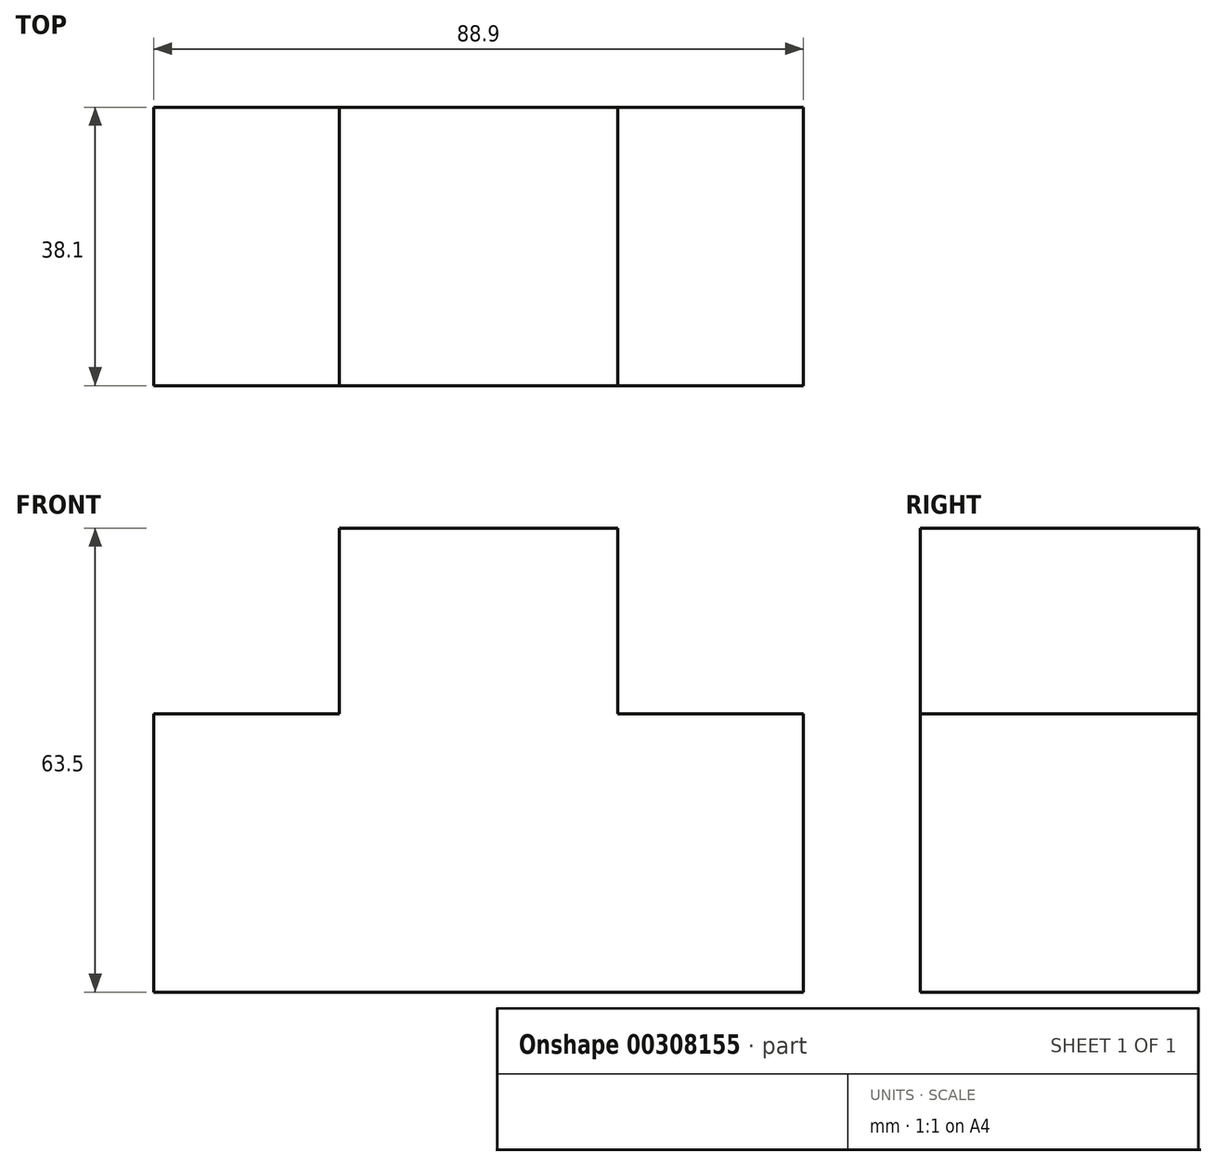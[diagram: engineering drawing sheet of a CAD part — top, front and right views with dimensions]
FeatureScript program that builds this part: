
annotation { "Feature Type Name" : "Feature", "Feature Type Description" : "" }
export const myFeature = defineFeature(function(context is Context, id is Id, definition is map)
    precondition{}
    {
        {
            var Q0;
            Q0=qCreatedBy(makeId("Front.planeOp"),FACE);
            var sketch = newSketch(context, id + "F0", { "sketchPlane" : qUnion([Q0])});
            skLineSegment(sketch, "E0", {"start": v(-39.89, -18.97) * mm, "end": v(49.01, -18.97) * mm});
            skLineSegment(sketch, "E1", {"start": v(-39.89, -18.97) * mm, "end": v(-39.89, 19.13) * mm});
            skLineSegment(sketch, "E2", {"start": v(-39.89, 19.13) * mm, "end": v(-14.49, 19.13) * mm});
            skLineSegment(sketch, "E3", {"start": v(-14.49, 19.13) * mm, "end": v(-14.49, 44.53) * mm});
            skLineSegment(sketch, "E4", {"start": v(-14.49, 44.53) * mm, "end": v(23.61, 44.53) * mm});
            skLineSegment(sketch, "E5", {"start": v(23.61, 44.53) * mm, "end": v(23.61, 19.13) * mm});
            skLineSegment(sketch, "E6", {"start": v(23.61, 19.13) * mm, "end": v(49.01, 19.13) * mm});
            skLineSegment(sketch, "E7", {"start": v(49.01, 19.13) * mm, "end": v(49.01, -18.97) * mm});
            skSolve(sketch);
        }
        {
            var Q0;
            Q0=makeQuery(id+"F0.imprint","IMPRINT",FACE,{"disambiguationData":[TD([[makeQuery(id+"F0.imprint","IMPRINT",EDGE,{"derivedFrom":sQuery(id+"F0.wireOp",EDGE,"E0")}),1.0]])]});
            extrude(context, id + "F1", {"entities" : qUnion([Q0]), "oppositeDirection" : true, "depth" : 38.1 * mm});
        }
    });
